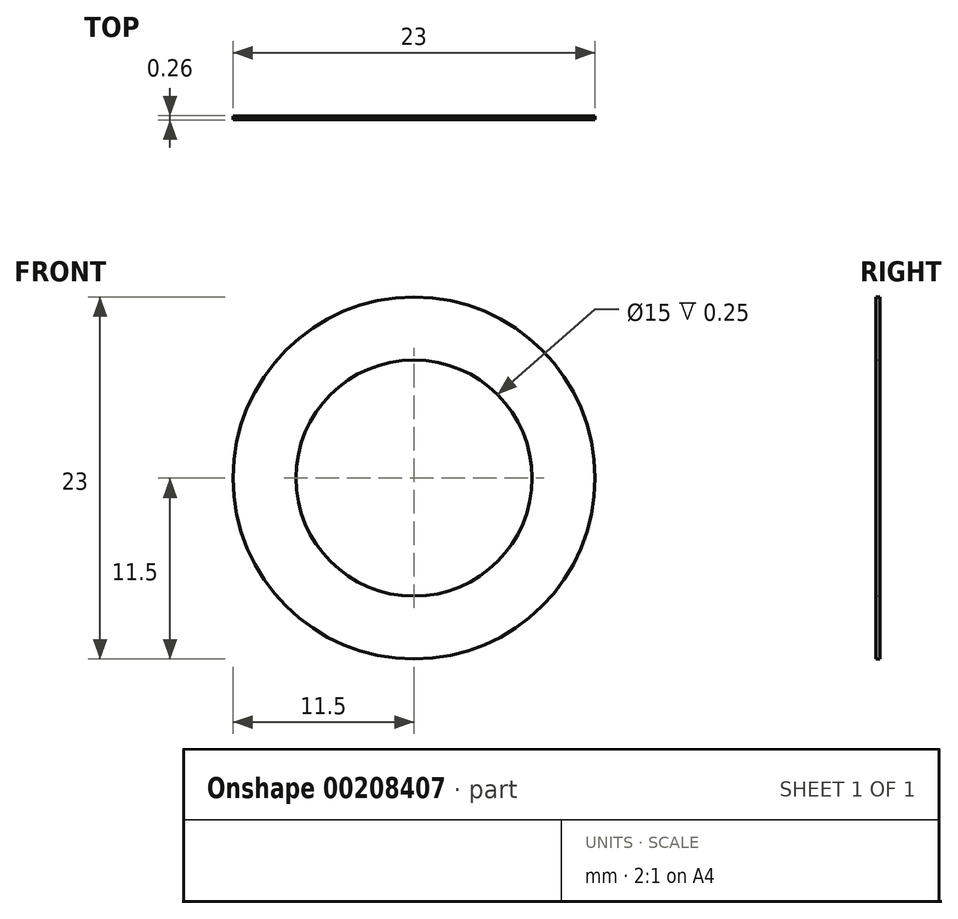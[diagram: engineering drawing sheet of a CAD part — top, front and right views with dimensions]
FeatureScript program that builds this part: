
annotation { "Feature Type Name" : "Feature", "Feature Type Description" : "" }
export const myFeature = defineFeature(function(context is Context, id is Id, definition is map)
    precondition{}
    {
        {
            var Q0;
            Q0=qCreatedBy(makeId("Front.planeOp"),FACE);
            var sketch = newSketch(context, id + "F0", { "sketchPlane" : qUnion([Q0])});
            skCircle(sketch, "E0", {"center": v(0, 0) * mm, "radius": 11.5 * mm});
            skCircle(sketch, "E1", {"center": v(0, 0) * mm, "radius": 7.5 * mm});
            skSolve(sketch);
        }
        {
            var Q0;
            Q0 = qSketchRegion(id + "F0", true);
            extrude(context, id + "F1", {"entities" : qUnion([Q0]), "depth" : 0.25 * mm, "symmetric" : true});
        }
    });
